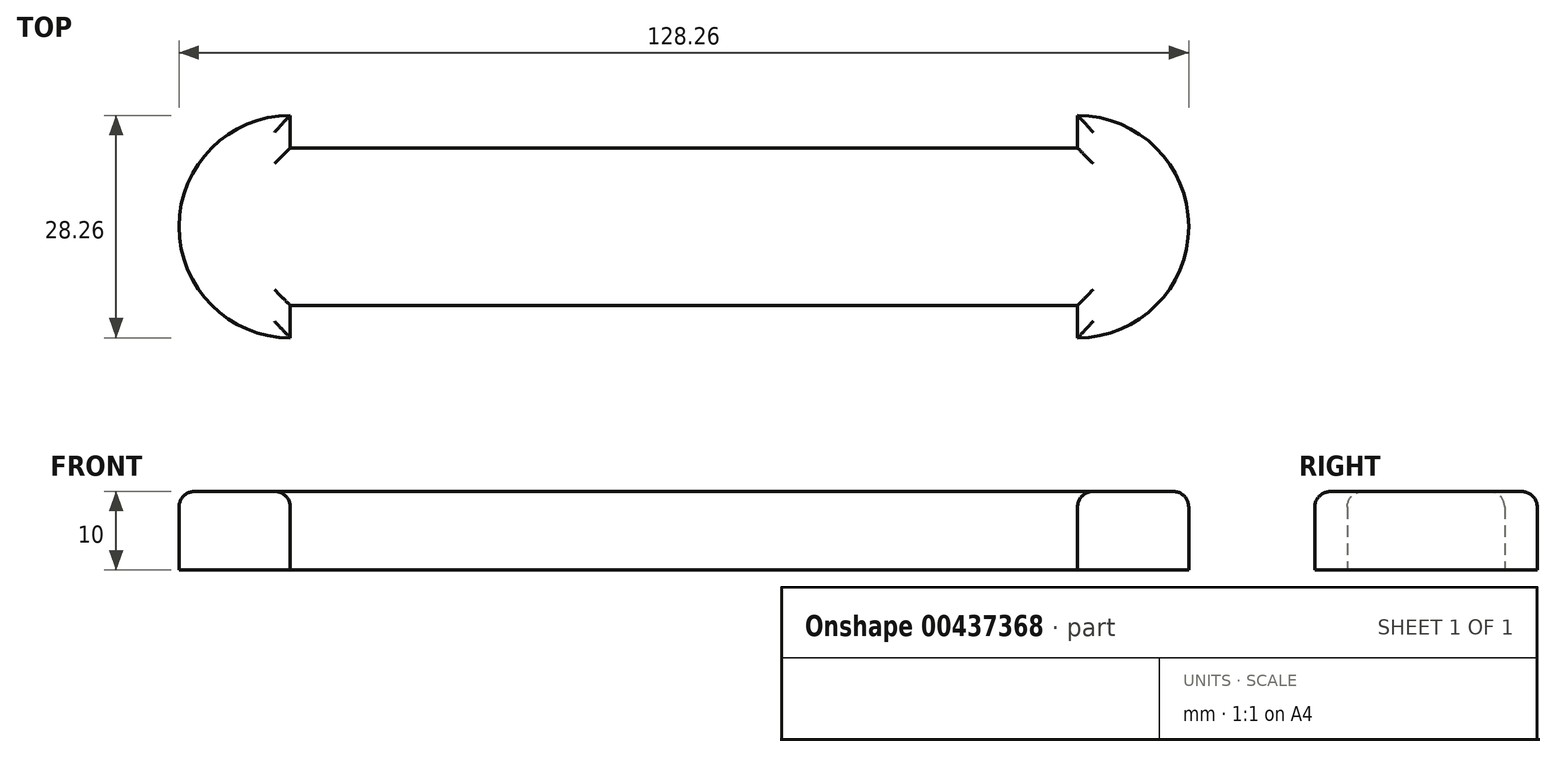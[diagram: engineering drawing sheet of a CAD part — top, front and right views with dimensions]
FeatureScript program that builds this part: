
annotation { "Feature Type Name" : "Feature", "Feature Type Description" : "" }
export const myFeature = defineFeature(function(context is Context, id is Id, definition is map)
    precondition{}
    {
        {
            var Q0;
            Q0=qCreatedBy(makeId("Top.planeOp"),FACE);
            var sketch = newSketch(context, id + "F0", { "sketchPlane" : qUnion([Q0])});
            skLineSegment(sketch, "E0.bottom", {"start": v(-45.13, 3.15) * mm, "end": v(54.87, 3.15) * mm});
            skLineSegment(sketch, "E0.top", {"start": v(-45.13, -16.85) * mm, "end": v(54.87, -16.85) * mm});
            skLineSegment(sketch, "E0.left", {"start": v(-45.13, 3.15) * mm, "end": v(-45.13, -16.85) * mm});
            skLineSegment(sketch, "E0.right", {"start": v(54.87, 3.15) * mm, "end": v(54.87, -16.85) * mm});
            skArc(sketch, "E1", {"start": v(54.87, -20.98) * mm, "mid": v(69, -6.85) * mm, "end": v(54.87, 7.28) * mm});
            skLineSegment(sketch, "E2", {"start": v(54.87, -16.85) * mm, "end": v(54.87, -20.98) * mm});
            skLineSegment(sketch, "E3", {"start": v(54.87, 3.15) * mm, "end": v(54.87, 7.28) * mm});
            skArc(sketch, "E4", {"start": v(-45.13, 7.28) * mm, "mid": v(-59.26, -6.85) * mm, "end": v(-45.13, -20.98) * mm});
            skLineSegment(sketch, "E5", {"start": v(-45.13, 3.15) * mm, "end": v(-45.13, 7.28) * mm});
            skLineSegment(sketch, "E6", {"start": v(-45.13, -16.85) * mm, "end": v(-45.13, -20.98) * mm});
            skSolve(sketch);
        }
        {
            var Q0;
            Q0=makeQuery(id+"F0.imprint","IMPRINT",FACE,{"disambiguationData":[TD([[makeQuery(id+"F0.imprint","IMPRINT",EDGE,{"derivedFrom":sQuery(id+"F0.wireOp",EDGE,"E0.left")}),-1.0]])]});
            var Q1;
            Q1=makeQuery(id+"F0.imprint","IMPRINT",FACE,{"disambiguationData":[TD([[makeQuery(id+"F0.imprint","IMPRINT",EDGE,{"derivedFrom":sQuery(id+"F0.wireOp",EDGE,"E0.bottom")}),-1.0]])]});
            var Q2;
            Q2=makeQuery(id+"F0.imprint","IMPRINT",FACE,{"disambiguationData":[TD([[makeQuery(id+"F0.imprint","IMPRINT",EDGE,{"derivedFrom":sQuery(id+"F0.wireOp",EDGE,"E0.right")}),1.0]])]});
            extrude(context, id + "F1", {"entities" : qUnion([Q0, Q1, Q2]), "depth" : 10 * mm});
        }
        {
            var Q0;
            Q0=makeQuery(id+"F1.opExtrude","CAP_EDGE",EDGE,{"disambiguationData":[OSD([sQuery(id+"F0.wireOp",EDGE,"E5")])],"isStart":false});
            var Q1;
            Q1=makeQuery(id+"F1.opExtrude","CAP_EDGE",EDGE,{"disambiguationData":[OSD([sQuery(id+"F0.wireOp",EDGE,"E6")])],"isStart":false});
            var Q2;
            Q2=makeQuery(id+"F1.opExtrude","CAP_EDGE",EDGE,{"disambiguationData":[OSD([sQuery(id+"F0.wireOp",EDGE,"E4")])],"isStart":false});
            var Q3;
            Q3=makeQuery(id+"F1.opExtrude","CAP_EDGE",EDGE,{"disambiguationData":[OSD([sQuery(id+"F0.wireOp",EDGE,"E0.bottom")])],"isStart":false});
            var Q4;
            Q4=makeQuery(id+"F1.opExtrude","CAP_EDGE",EDGE,{"disambiguationData":[OSD([sQuery(id+"F0.wireOp",EDGE,"E0.top")])],"isStart":false});
            var Q5;
            Q5=makeQuery(id+"F1.opExtrude","CAP_FACE",FACE,{"disambiguationData":[OSD([sQuery(id+"F0.wireOp",EDGE,"E0.bottom"),sQuery(id+"F0.wireOp",EDGE,"E0.top"),sQuery(id+"F0.wireOp",EDGE,"E1"),sQuery(id+"F0.wireOp",EDGE,"E2"),sQuery(id+"F0.wireOp",EDGE,"E3"),sQuery(id+"F0.wireOp",EDGE,"E4"),sQuery(id+"F0.wireOp",EDGE,"E5"),sQuery(id+"F0.wireOp",EDGE,"E6")])],"isStart":false});
            fillet(context, id + "F2", {"entities" : qUnion([Q0, Q1, Q2, Q3, Q4, Q5]), "radius" : 2 * mm, "tangentPropagation" : true, "allowEdgeOverflow" : false});
        }
    });
